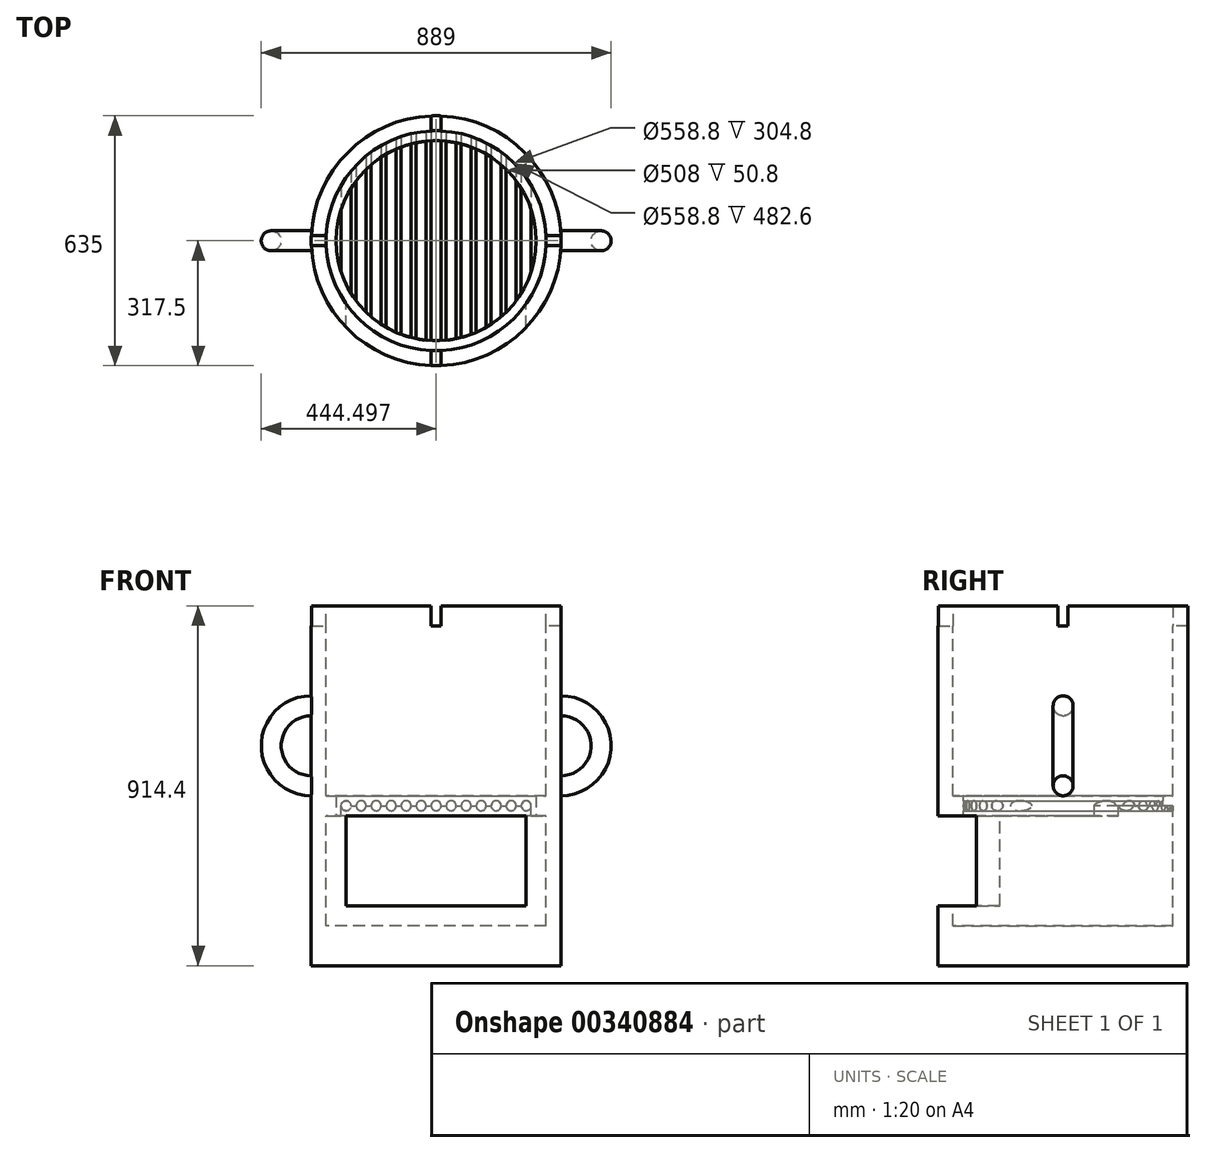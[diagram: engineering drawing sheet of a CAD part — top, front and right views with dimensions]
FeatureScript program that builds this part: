
annotation { "Feature Type Name" : "Feature", "Feature Type Description" : "" }
export const myFeature = defineFeature(function(context is Context, id is Id, definition is map)
    precondition{}
    {
        {
            var Q0;
            Q0=qCreatedBy(makeId("Top.planeOp"),FACE);
            var sketch = newSketch(context, id + "F0", { "sketchPlane" : qUnion([Q0])});
            skCircle(sketch, "E0", {"center": v(0, 0) * mm, "radius": 158.75 * mm});
            skSolve(sketch);
        }
        {
            var Q0;
            Q0=makeQuery(id+"F0.imprint","IMPRINT",FACE,{"disambiguationData":[TD([[makeQuery(id+"F0.imprint","IMPRINT",EDGE,{"derivedFrom":sQuery(id+"F0.wireOp",EDGE,"E0")}),1.0]])]});
            extrude(context, id + "F1", {"entities" : qUnion([Q0]), "depth" : 457.2 * mm});
        }
        {
            var Q0;
            Q0=makeQuery(id+"F1.opExtrude","CAP_FACE",FACE,{"disambiguationData":[OSD([sQuery(id+"F0.wireOp",EDGE,"E0")])],"isStart":false});
            var sketch = newSketch(context, id + "F2", { "sketchPlane" : qUnion([Q0])});
            skPoint(sketch, "E1.0", {"position": v(0, 0) * mm});
            skCircle(sketch, "E2", {"center": v(0, 0) * mm, "radius": 139.7 * mm});
            skSolve(sketch);
        }
        {
            var Q0;
            Q0=makeQuery(id+"F2.imprint","IMPRINT",FACE,{"disambiguationData":[TD([[makeQuery(id+"F2.imprint","IMPRINT",EDGE,{"derivedFrom":sQuery(id+"F2.wireOp",EDGE,"E2")}),1.0]])]});
            extrude(context, id + "F3", {"entities" : qUnion([Q0]), "operationType" : NewBodyOperationType.REMOVE, "oppositeDirection" : true, "depth" : 406.4 * mm});
        }
        {
            var Q0;
            Q0=qCreatedBy(makeId("Front.planeOp"),FACE);
            var sketch = newSketch(context, id + "F4", { "sketchPlane" : qUnion([Q0])});
            skLineSegment(sketch, "E3", {"start": v(-158.75, 0) * mm, "end": v(-158.75, 457.2) * mm});
            skLineSegment(sketch, "E4", {"start": v(158.75, 457.2) * mm, "end": v(158.75, 0) * mm});
            skLineSegment(sketch, "E5", {"start": v(158.75, 457.2) * mm, "end": v(-158.75, 457.2) * mm});
            skLineSegment(sketch, "E6", {"start": v(158.75, 0) * mm, "end": v(-158.75, 0) * mm});
            skPoint(sketch, "E7", {"position": v(0, 0) * mm});
            skLineSegment(sketch, "E8", {"start": v(0, 457.2) * mm, "end": v(0, 0) * mm, "construction": true});
            skLineSegment(sketch, "E9.bottom", {"start": v(114.3, 203.2) * mm, "end": v(-114.3, 203.2) * mm});
            skLineSegment(sketch, "E9.top", {"start": v(114.3, 76.2) * mm, "end": v(-114.3, 76.2) * mm});
            skLineSegment(sketch, "E9.left", {"start": v(114.3, 203.2) * mm, "end": v(114.3, 76.2) * mm});
            skLineSegment(sketch, "E9.right", {"start": v(-114.3, 203.2) * mm, "end": v(-114.3, 76.2) * mm});
            skPoint(sketch, "E10", {"position": v(-514.73, 96.28) * mm});
            skSolve(sketch);
        }
        {
            var Q0;
            Q0=makeQuery(id+"F4.imprint","IMPRINT",FACE,{"disambiguationData":[TD([[makeQuery(id+"F4.imprint","IMPRINT",EDGE,{"derivedFrom":sQuery(id+"F4.wireOp",EDGE,"E9.bottom")}),1.0]])]});
            extrude(context, id + "F5", {"entities" : qUnion([Q0]), "operationType" : NewBodyOperationType.REMOVE, "depth" : 177.8 * mm});
        }
        {
            var Q0;
            Q0=makeQuery(id+"F1.opExtrude","CAP_FACE",FACE,{"disambiguationData":[OSD([sQuery(id+"F0.wireOp",EDGE,"E0")])],"isStart":false});
            var sketch = newSketch(context, id + "F6", { "sketchPlane" : qUnion([Q0])});
            skCircle(sketch, "E11.0.0", {"center": v(0, 0) * mm, "radius": 158.75 * mm, "construction": true});
            skCircle(sketch, "E12.0", {"center": v(0, 0) * mm, "radius": 139.7 * mm, "construction": true});
            skLineSegment(sketch, "E13", {"start": v(-158.75, 0) * mm, "end": v(158.75, 0) * mm, "construction": true});
            skLineSegment(sketch, "E14", {"start": v(0, 158.75) * mm, "end": v(0, -158.75) * mm, "construction": true});
            skLineSegment(sketch, "E15.bottom", {"start": v(-6.35, 158.75) * mm, "end": v(6.35, 158.75) * mm});
            skLineSegment(sketch, "E15.top", {"start": v(-6.35, 139.56) * mm, "end": v(6.35, 139.56) * mm});
            skLineSegment(sketch, "E15.left", {"start": v(-6.35, 158.75) * mm, "end": v(-6.35, 139.56) * mm});
            skLineSegment(sketch, "E15.right", {"start": v(6.35, 158.75) * mm, "end": v(6.35, 139.56) * mm});
            skLineSegment(sketch, "E16.bottom", {"start": v(-158.75, -6.35) * mm, "end": v(-139.56, -6.35) * mm});
            skLineSegment(sketch, "E16.top", {"start": v(-158.75, 6.35) * mm, "end": v(-139.56, 6.35) * mm});
            skLineSegment(sketch, "E16.left", {"start": v(-158.75, -6.35) * mm, "end": v(-158.75, 6.35) * mm});
            skLineSegment(sketch, "E16.right", {"start": v(-139.56, -6.35) * mm, "end": v(-139.56, 6.35) * mm});
            skLineSegment(sketch, "E17.bottom", {"start": v(158.75, 6.35) * mm, "end": v(139.56, 6.35) * mm});
            skLineSegment(sketch, "E17.top", {"start": v(158.75, -6.35) * mm, "end": v(139.56, -6.35) * mm});
            skLineSegment(sketch, "E17.left", {"start": v(158.75, 6.35) * mm, "end": v(158.75, -6.35) * mm});
            skLineSegment(sketch, "E17.right", {"start": v(139.56, 6.35) * mm, "end": v(139.56, -6.35) * mm});
            skLineSegment(sketch, "E18.bottom", {"start": v(6.35, -158.75) * mm, "end": v(-6.35, -158.75) * mm});
            skLineSegment(sketch, "E18.top", {"start": v(6.35, -139.56) * mm, "end": v(-6.35, -139.56) * mm});
            skLineSegment(sketch, "E18.left", {"start": v(6.35, -158.75) * mm, "end": v(6.35, -139.56) * mm});
            skLineSegment(sketch, "E18.right", {"start": v(-6.35, -158.75) * mm, "end": v(-6.35, -139.56) * mm});
            skSolve(sketch);
        }
        {
            var Q0;
            {var subQ0=makeQuery(id+"F1.opExtrude","CAP_EDGE",EDGE,{"disambiguationData":[OSD([sQuery(id+"F0.wireOp",EDGE,"E0")])],"isStart":false});var subQ1=makeQuery(id+"F6.imprint","INTERSECT",VERTEX,{"derivedFrom":[subQ0,sQuery(id+"F6.wireOp",EDGE,"E15.bottom")]});Q0=makeQuery(id+"F6.imprint","IMPRINT",FACE,{"disambiguationData":[TD([[makeQuery(id+"F6.imprint","IMPRINT",EDGE,{"disambiguationData":[TD([[subQ1,-1.0]])],"derivedFrom":subQ0}),1.0]])]});}
            var Q1;
            {var subQ0=sQuery(id+"F6.wireOp",EDGE,"E16.bottom");var subQ1=makeQuery(id+"F1.opExtrude","CAP_EDGE",EDGE,{"disambiguationData":[OSD([sQuery(id+"F0.wireOp",EDGE,"E0")])],"isStart":false});var subQ2=makeQuery(id+"F6.imprint","INTERSECT",VERTEX,{"derivedFrom":[subQ1,subQ0]});Q1=makeQuery(id+"F6.imprint","IMPRINT",FACE,{"disambiguationData":[TD([[makeQuery(id+"F6.imprint","IMPRINT",EDGE,{"disambiguationData":[TD([[subQ2,1.0]])],"derivedFrom":subQ1}),1.0]])]});}
            var Q2;
            {var subQ0=makeQuery(id+"F1.opExtrude","CAP_EDGE",EDGE,{"disambiguationData":[OSD([sQuery(id+"F0.wireOp",EDGE,"E0")])],"isStart":false});var subQ1=makeQuery(id+"F6.imprint","INTERSECT",VERTEX,{"derivedFrom":[subQ0,sQuery(id+"F6.wireOp",EDGE,"E18.bottom")]});Q2=makeQuery(id+"F6.imprint","IMPRINT",FACE,{"disambiguationData":[TD([[makeQuery(id+"F6.imprint","IMPRINT",EDGE,{"disambiguationData":[TD([[subQ1,-1.0]])],"derivedFrom":subQ0}),1.0]])]});}
            var Q3;
            {var subQ0=sQuery(id+"F6.wireOp",EDGE,"E17.bottom");var subQ1=makeQuery(id+"F1.opExtrude","CAP_EDGE",EDGE,{"disambiguationData":[OSD([sQuery(id+"F0.wireOp",EDGE,"E0")])],"isStart":false});var subQ2=makeQuery(id+"F6.imprint","INTERSECT",VERTEX,{"derivedFrom":[subQ1,subQ0]});Q3=makeQuery(id+"F6.imprint","IMPRINT",FACE,{"disambiguationData":[TD([[makeQuery(id+"F6.imprint","IMPRINT",EDGE,{"disambiguationData":[TD([[subQ2,1.0]])],"derivedFrom":subQ1}),1.0]])]});}
            extrude(context, id + "F7", {"entities" : qUnion([Q0, Q1, Q2, Q3]), "operationType" : NewBodyOperationType.REMOVE, "oppositeDirection" : true, "depth" : 25.4 * mm});
        }
        {
            var Q0;
            Q0=makeQuery(id+"F5.boolean.opBoolean","COPY",FACE,{"derivedFrom":makeQuery(id+"F5.opExtrude","SWEPT_FACE",FACE,{"disambiguationData":[OSD([sQuery(id+"F4.wireOp",EDGE,"E9.bottom")])]})});
            var sketch = newSketch(context, id + "F8", { "sketchPlane" : qUnion([Q0])});
            skCircle(sketch, "E19.0.0", {"center": v(0, 0) * mm, "radius": 139.7 * mm});
            skLineSegment(sketch, "E20.0.0", {"start": v(139.56, 6.35) * mm, "end": v(158.62, 6.35) * mm});
            skArc(sketch, "E20.0.1", {"start": v(158.62, 6.35) * mm, "mid": v(158.72, 3.18) * mm, "end": v(158.75, 0) * mm});
            skArc(sketch, "E20.0.2", {"start": v(158.75, 0) * mm, "mid": v(158.72, -3.18) * mm, "end": v(158.62, -6.35) * mm});
            skLineSegment(sketch, "E20.0.3", {"start": v(158.62, -6.35) * mm, "end": v(139.56, -6.35) * mm});
            skArc(sketch, "E20.0.4", {"start": v(139.56, -6.35) * mm, "mid": v(139.7, 0) * mm, "end": v(139.56, 6.35) * mm});
            skLineSegment(sketch, "E21.0.0", {"start": v(6.35, -139.56) * mm, "end": v(6.35, -158.62) * mm});
            skArc(sketch, "E21.0.1", {"start": v(6.35, -158.62) * mm, "mid": v(3.18, -158.72) * mm, "end": v(0, -158.75) * mm});
            skArc(sketch, "E21.0.2", {"start": v(0, -158.75) * mm, "mid": v(-3.18, -158.72) * mm, "end": v(-6.35, -158.62) * mm});
            skLineSegment(sketch, "E21.0.3", {"start": v(-6.35, -158.62) * mm, "end": v(-6.35, -139.56) * mm});
            skArc(sketch, "E21.0.4", {"start": v(-6.35, -139.56) * mm, "mid": v(0, -139.7) * mm, "end": v(6.35, -139.56) * mm});
            skLineSegment(sketch, "E22.0.0", {"start": v(-6.35, 139.56) * mm, "end": v(-6.35, 158.62) * mm});
            skArc(sketch, "E22.0.1", {"start": v(-6.35, 158.62) * mm, "mid": v(-3.18, 158.72) * mm, "end": v(0, 158.75) * mm});
            skArc(sketch, "E22.0.2", {"start": v(0, 158.75) * mm, "mid": v(3.18, 158.72) * mm, "end": v(6.35, 158.62) * mm});
            skLineSegment(sketch, "E22.0.3", {"start": v(6.35, 158.62) * mm, "end": v(6.35, 139.56) * mm});
            skArc(sketch, "E22.0.4", {"start": v(6.35, 139.56) * mm, "mid": v(0, 139.7) * mm, "end": v(-6.35, 139.56) * mm});
            skLineSegment(sketch, "E23.0.0", {"start": v(-139.56, -6.35) * mm, "end": v(-158.62, -6.35) * mm});
            skArc(sketch, "E23.0.1", {"start": v(-158.62, -6.35) * mm, "mid": v(-158.72, -3.18) * mm, "end": v(-158.75, 0) * mm});
            skArc(sketch, "E23.0.2", {"start": v(-158.75, 0) * mm, "mid": v(-158.72, 3.18) * mm, "end": v(-158.62, 6.35) * mm});
            skLineSegment(sketch, "E23.0.3", {"start": v(-158.62, 6.35) * mm, "end": v(-139.56, 6.35) * mm});
            skArc(sketch, "E23.0.4", {"start": v(-139.56, 6.35) * mm, "mid": v(-139.7, 0) * mm, "end": v(-139.56, -6.35) * mm});
            skLineSegment(sketch, "E24", {"start": v(-139.56, 0) * mm, "end": v(139.7, 0) * mm, "construction": true});
            skPoint(sketch, "E24.startSnap0", {"position": v(-139.7, 0) * mm});
            skCircle(sketch, "E25", {"center": v(0, 0) * mm, "radius": 127 * mm});
            skLineSegment(sketch, "E26", {"start": v(0, 127) * mm, "end": v(0, -127) * mm});
            skPoint(sketch, "E27", {"position": v(127, 0) * mm});
            skPoint(sketch, "E28", {"position": v(-127, 0) * mm});
            skPoint(sketch, "E29", {"position": v(-76.2, 0) * mm});
            skPoint(sketch, "E30", {"position": v(-19.05, 0) * mm});
            skPoint(sketch, "E31", {"position": v(-38.1, 0) * mm});
            skPoint(sketch, "E32", {"position": v(-57.15, 0) * mm});
            skPoint(sketch, "E33", {"position": v(-95.25, 0) * mm});
            skPoint(sketch, "E34", {"position": v(-114.3, 0) * mm});
            skLineSegment(sketch, "E35", {"start": v(-114.3, 55.36) * mm, "end": v(-114.3, -55.36) * mm});
            skLineSegment(sketch, "E36", {"start": v(-95.25, 84) * mm, "end": v(-95.25, -84) * mm});
            skLineSegment(sketch, "E37", {"start": v(-76.2, 101.6) * mm, "end": v(-76.2, -101.6) * mm});
            skLineSegment(sketch, "E38", {"start": v(-57.15, -113.41) * mm, "end": v(-57.15, 113.41) * mm});
            skLineSegment(sketch, "E39", {"start": v(-38.1, -121.15) * mm, "end": v(-38.1, 121.15) * mm});
            skLineSegment(sketch, "E40", {"start": v(-19.05, -125.56) * mm, "end": v(-19.05, 125.56) * mm});
            skLineSegment(sketch, "E41.MirrorCS", {"start": v(0, -121.15) * mm, "end": v(0, 121.15) * mm});
            skLineSegment(sketch, "E42.MirrorCS", {"start": v(19.05, -125.56) * mm, "end": v(19.05, 125.56) * mm});
            skLineSegment(sketch, "E43.MirrorCS", {"start": v(38.1, -121.15) * mm, "end": v(38.1, 121.15) * mm});
            skLineSegment(sketch, "E44.MirrorCS", {"start": v(57.15, -113.41) * mm, "end": v(57.15, 113.41) * mm});
            skLineSegment(sketch, "E45.MirrorCS", {"start": v(76.2, 101.6) * mm, "end": v(76.2, -101.6) * mm});
            skLineSegment(sketch, "E46.MirrorCS", {"start": v(95.25, 84) * mm, "end": v(95.25, -84) * mm});
            skLineSegment(sketch, "E47.MirrorCS", {"start": v(114.3, 55.36) * mm, "end": v(114.3, -55.36) * mm});
            skSolve(sketch);
        }
        {
            var Q0;
            {var subQ17=sQuery(id+"F8.wireOp",EDGE,"E19.0.0");var subQ19=makeQuery(id+"F8.imprint","INTERSECT",VERTEX,{"derivedFrom":[subQ17,sQuery(id+"F8.wireOp",EDGE,"E23.0.0")]});Q0=makeQuery(id+"F8.imprint","IMPRINT",FACE,{"disambiguationData":[TD([[makeQuery(id+"F8.imprint","IMPRINT",EDGE,{"disambiguationData":[TD([[subQ19,1.0]])],"derivedFrom":subQ17}),1.0]])]});}
            extrude(context, id + "F9", {"entities" : qUnion([Q0]), "operationType" : NewBodyOperationType.ADD, "oppositeDirection" : true, "depth" : 12.7 * mm});
        }
        {
            var Q0;
            Q0=qCreatedBy(makeId("Front.planeOp"),FACE);
            var sketch = newSketch(context, id + "F10", { "sketchPlane" : qUnion([Q0])});
            skPoint(sketch, "E48.0", {"position": v(-114.3, 203.2) * mm});
            skPoint(sketch, "E49.0", {"position": v(-95.25, 203.2) * mm});
            skPoint(sketch, "E50.0", {"position": v(-76.2, 203.2) * mm});
            skPoint(sketch, "E51.0", {"position": v(-57.15, 203.2) * mm});
            skPoint(sketch, "E52.0", {"position": v(-38.1, 203.2) * mm});
            skPoint(sketch, "E53.0", {"position": v(-19.05, 203.2) * mm});
            skPoint(sketch, "E54.0", {"position": v(0, 203.2) * mm});
            skPoint(sketch, "E55.0", {"position": v(19.05, 203.2) * mm});
            skPoint(sketch, "E56.0", {"position": v(38.1, 203.2) * mm});
            skPoint(sketch, "E57.0", {"position": v(57.15, 203.2) * mm});
            skPoint(sketch, "E58.0", {"position": v(76.2, 203.2) * mm});
            skPoint(sketch, "E59.0", {"position": v(95.25, 203.2) * mm});
            skPoint(sketch, "E60.0", {"position": v(114.3, 203.2) * mm});
            skCircle(sketch, "E61", {"center": v(-114.3, 203.2) * mm, "radius": 6.35 * mm});
            skCircle(sketch, "E62", {"center": v(-95.25, 203.2) * mm, "radius": 6.35 * mm});
            skCircle(sketch, "E63", {"center": v(-76.2, 203.2) * mm, "radius": 6.35 * mm});
            skCircle(sketch, "E64", {"center": v(-57.15, 203.2) * mm, "radius": 6.35 * mm});
            skCircle(sketch, "E65", {"center": v(-38.1, 203.2) * mm, "radius": 6.35 * mm});
            skCircle(sketch, "E66", {"center": v(-19.05, 203.2) * mm, "radius": 6.35 * mm});
            skCircle(sketch, "E67", {"center": v(0, 203.2) * mm, "radius": 6.35 * mm});
            skCircle(sketch, "E68", {"center": v(19.05, 203.2) * mm, "radius": 6.35 * mm});
            skCircle(sketch, "E69", {"center": v(38.1, 203.2) * mm, "radius": 6.35 * mm});
            skCircle(sketch, "E70", {"center": v(57.15, 203.2) * mm, "radius": 6.35 * mm});
            skCircle(sketch, "E71", {"center": v(76.2, 203.2) * mm, "radius": 6.35 * mm});
            skCircle(sketch, "E72", {"center": v(95.25, 203.2) * mm, "radius": 6.35 * mm});
            skCircle(sketch, "E73", {"center": v(114.3, 203.2) * mm, "radius": 6.35 * mm});
            skSolve(sketch);
        }
        {
            var Q0;
            Q0=makeQuery(id+"F10.imprint","IMPRINT",FACE,{"disambiguationData":[TD([[makeQuery(id+"F10.imprint","IMPRINT",EDGE,{"derivedFrom":sQuery(id+"F10.wireOp",EDGE,"E61")}),1.0]])]});
            var Q1;
            Q1=makeQuery(id+"F10.imprint","IMPRINT",FACE,{"disambiguationData":[TD([[makeQuery(id+"F10.imprint","IMPRINT",EDGE,{"derivedFrom":sQuery(id+"F10.wireOp",EDGE,"E66")}),1.0]])]});
            var Q2;
            Q2=makeQuery(id+"F10.imprint","IMPRINT",FACE,{"disambiguationData":[TD([[makeQuery(id+"F10.imprint","IMPRINT",EDGE,{"derivedFrom":sQuery(id+"F10.wireOp",EDGE,"E62")}),1.0]])]});
            var Q3;
            Q3=makeQuery(id+"F10.imprint","IMPRINT",FACE,{"disambiguationData":[TD([[makeQuery(id+"F10.imprint","IMPRINT",EDGE,{"derivedFrom":sQuery(id+"F10.wireOp",EDGE,"E63")}),1.0]])]});
            var Q4;
            Q4=makeQuery(id+"F10.imprint","IMPRINT",FACE,{"disambiguationData":[TD([[makeQuery(id+"F10.imprint","IMPRINT",EDGE,{"derivedFrom":sQuery(id+"F10.wireOp",EDGE,"E65")}),1.0]])]});
            var Q5;
            Q5=makeQuery(id+"F10.imprint","IMPRINT",FACE,{"disambiguationData":[TD([[makeQuery(id+"F10.imprint","IMPRINT",EDGE,{"derivedFrom":sQuery(id+"F10.wireOp",EDGE,"E64")}),1.0]])]});
            var Q6;
            Q6=makeQuery(id+"F10.imprint","IMPRINT",FACE,{"disambiguationData":[TD([[makeQuery(id+"F10.imprint","IMPRINT",EDGE,{"derivedFrom":sQuery(id+"F10.wireOp",EDGE,"E72")}),1.0]])]});
            var Q7;
            Q7=makeQuery(id+"F10.imprint","IMPRINT",FACE,{"disambiguationData":[TD([[makeQuery(id+"F10.imprint","IMPRINT",EDGE,{"derivedFrom":sQuery(id+"F10.wireOp",EDGE,"E71")}),1.0]])]});
            var Q8;
            Q8=makeQuery(id+"F10.imprint","IMPRINT",FACE,{"disambiguationData":[TD([[makeQuery(id+"F10.imprint","IMPRINT",EDGE,{"derivedFrom":sQuery(id+"F10.wireOp",EDGE,"E70")}),1.0]])]});
            var Q9;
            Q9=makeQuery(id+"F10.imprint","IMPRINT",FACE,{"disambiguationData":[TD([[makeQuery(id+"F10.imprint","IMPRINT",EDGE,{"derivedFrom":sQuery(id+"F10.wireOp",EDGE,"E69")}),1.0]])]});
            var Q10;
            Q10=makeQuery(id+"F10.imprint","IMPRINT",FACE,{"disambiguationData":[TD([[makeQuery(id+"F10.imprint","IMPRINT",EDGE,{"derivedFrom":sQuery(id+"F10.wireOp",EDGE,"E68")}),1.0]])]});
            var Q11;
            Q11=makeQuery(id+"F10.imprint","IMPRINT",FACE,{"disambiguationData":[TD([[makeQuery(id+"F10.imprint","IMPRINT",EDGE,{"derivedFrom":sQuery(id+"F10.wireOp",EDGE,"E67")}),1.0]])]});
            var Q12;
            Q12=makeQuery(id+"F10.imprint","IMPRINT",FACE,{"disambiguationData":[TD([[makeQuery(id+"F10.imprint","IMPRINT",EDGE,{"derivedFrom":sQuery(id+"F10.wireOp",EDGE,"E73")}),1.0]])]});
            var Q13;
            Q13=makeQuery(id+"F9.opExtrude","SWEPT_FACE",FACE,{"disambiguationData":[OSD([sQuery(id+"F8.wireOp",EDGE,"E25")])]});
            extrude(context, id + "F11", {"entities" : qUnion([Q0, Q1, Q2, Q3, Q4, Q5, Q6, Q7, Q8, Q9, Q10, Q11, Q12]), "operationType" : NewBodyOperationType.ADD, "endBound" : BoundingType.UP_TO_SURFACE, "endBoundEntityFace" : qUnion([Q13]), "depth" : 228.6 * mm});
        }
        {
            var Q0;
            Q0=makeQuery(id+"F10.imprint","IMPRINT",FACE,{"disambiguationData":[TD([[makeQuery(id+"F10.imprint","IMPRINT",EDGE,{"derivedFrom":sQuery(id+"F10.wireOp",EDGE,"E73")}),1.0]])]});
            var Q1;
            Q1=makeQuery(id+"F10.imprint","IMPRINT",FACE,{"disambiguationData":[TD([[makeQuery(id+"F10.imprint","IMPRINT",EDGE,{"derivedFrom":sQuery(id+"F10.wireOp",EDGE,"E72")}),1.0]])]});
            var Q2;
            Q2=makeQuery(id+"F10.imprint","IMPRINT",FACE,{"disambiguationData":[TD([[makeQuery(id+"F10.imprint","IMPRINT",EDGE,{"derivedFrom":sQuery(id+"F10.wireOp",EDGE,"E71")}),1.0]])]});
            var Q3;
            Q3=makeQuery(id+"F10.imprint","IMPRINT",FACE,{"disambiguationData":[TD([[makeQuery(id+"F10.imprint","IMPRINT",EDGE,{"derivedFrom":sQuery(id+"F10.wireOp",EDGE,"E70")}),1.0]])]});
            var Q4;
            Q4=makeQuery(id+"F10.imprint","IMPRINT",FACE,{"disambiguationData":[TD([[makeQuery(id+"F10.imprint","IMPRINT",EDGE,{"derivedFrom":sQuery(id+"F10.wireOp",EDGE,"E69")}),1.0]])]});
            var Q5;
            Q5=makeQuery(id+"F10.imprint","IMPRINT",FACE,{"disambiguationData":[TD([[makeQuery(id+"F10.imprint","IMPRINT",EDGE,{"derivedFrom":sQuery(id+"F10.wireOp",EDGE,"E68")}),1.0]])]});
            var Q6;
            Q6=makeQuery(id+"F10.imprint","IMPRINT",FACE,{"disambiguationData":[TD([[makeQuery(id+"F10.imprint","IMPRINT",EDGE,{"derivedFrom":sQuery(id+"F10.wireOp",EDGE,"E67")}),1.0]])]});
            var Q7;
            Q7=makeQuery(id+"F10.imprint","IMPRINT",FACE,{"disambiguationData":[TD([[makeQuery(id+"F10.imprint","IMPRINT",EDGE,{"derivedFrom":sQuery(id+"F10.wireOp",EDGE,"E61")}),1.0]])]});
            var Q8;
            Q8=makeQuery(id+"F10.imprint","IMPRINT",FACE,{"disambiguationData":[TD([[makeQuery(id+"F10.imprint","IMPRINT",EDGE,{"derivedFrom":sQuery(id+"F10.wireOp",EDGE,"E66")}),1.0]])]});
            var Q9;
            Q9=makeQuery(id+"F10.imprint","IMPRINT",FACE,{"disambiguationData":[TD([[makeQuery(id+"F10.imprint","IMPRINT",EDGE,{"derivedFrom":sQuery(id+"F10.wireOp",EDGE,"E62")}),1.0]])]});
            var Q10;
            Q10=makeQuery(id+"F10.imprint","IMPRINT",FACE,{"disambiguationData":[TD([[makeQuery(id+"F10.imprint","IMPRINT",EDGE,{"derivedFrom":sQuery(id+"F10.wireOp",EDGE,"E63")}),1.0]])]});
            var Q11;
            Q11=makeQuery(id+"F10.imprint","IMPRINT",FACE,{"disambiguationData":[TD([[makeQuery(id+"F10.imprint","IMPRINT",EDGE,{"derivedFrom":sQuery(id+"F10.wireOp",EDGE,"E65")}),1.0]])]});
            var Q12;
            Q12=makeQuery(id+"F10.imprint","IMPRINT",FACE,{"disambiguationData":[TD([[makeQuery(id+"F10.imprint","IMPRINT",EDGE,{"derivedFrom":sQuery(id+"F10.wireOp",EDGE,"E64")}),1.0]])]});
            extrude(context, id + "F12", {"entities" : qUnion([Q0, Q1, Q2, Q3, Q4, Q5, Q6, Q7, Q8, Q9, Q10, Q11, Q12]), "operationType" : NewBodyOperationType.ADD, "endBound" : BoundingType.UP_TO_NEXT, "oppositeDirection" : true, "depth" : 25.4 * mm});
        }
        {
            var Q0;
            {var subQ0=sQuery(id+"F10.wireOp",EDGE,"E63");var subQ1=sQuery(id+"F8.wireOp",EDGE,"E25");var subQ2=sQuery(id+"F10.wireOp",EDGE,"E73");var subQ3=sQuery(id+"F10.wireOp",EDGE,"E72");var subQ4=sQuery(id+"F10.wireOp",EDGE,"E71");var subQ5=sQuery(id+"F10.wireOp",EDGE,"E69");var subQ6=sQuery(id+"F10.wireOp",EDGE,"E68");var subQ7=sQuery(id+"F10.wireOp",EDGE,"E67");var subQ8=sQuery(id+"F10.wireOp",EDGE,"E66");var subQ9=sQuery(id+"F10.wireOp",EDGE,"E61");var subQ10=sQuery(id+"F10.wireOp",EDGE,"E64");var subQ11=sQuery(id+"F10.wireOp",EDGE,"E70");var subQ12=sQuery(id+"F10.wireOp",EDGE,"E62");var subQ13=sQuery(id+"F10.wireOp",EDGE,"E65");Q0=makeQuery(id+"F12.boolean.opBoolean","SPLIT",FACE,{"disambiguationData":[TD([makeQuery(id+"F1.opExtrude","SWEPT_FACE",FACE,{"disambiguationData":[OSD([sQuery(id+"F0.wireOp",EDGE,"E0")])]}),makeQuery(id+"F3.boolean.opBoolean","COPY",FACE,{"derivedFrom":makeQuery(id+"F3.opExtrude","SWEPT_FACE",FACE,{"disambiguationData":[OSD([sQuery(id+"F2.wireOp",EDGE,"E2")])]})}),makeQuery(id+"F5.boolean.opBoolean","COPY",FACE,{"derivedFrom":makeQuery(id+"F5.opExtrude","SWEPT_FACE",FACE,{"disambiguationData":[OSD([sQuery(id+"F4.wireOp",EDGE,"E9.left")])]})}),makeQuery(id+"F5.boolean.opBoolean","COPY",FACE,{"derivedFrom":makeQuery(id+"F5.opExtrude","SWEPT_FACE",FACE,{"disambiguationData":[OSD([sQuery(id+"F4.wireOp",EDGE,"E9.right")])]})}),makeQuery(id+"F9.opExtrude","SWEPT_FACE",FACE,{"disambiguationData":[OSD([subQ1])]}),makeQuery(id+"F11.opExtrude","SWEPT_FACE",FACE,{"disambiguationData":[OSD([subQ9])]}),makeQuery(id+"F11.opExtrude","SWEPT_FACE",FACE,{"disambiguationData":[OSD([subQ12])]}),makeQuery(id+"F11.opExtrude","SWEPT_FACE",FACE,{"disambiguationData":[OSD([subQ0])]}),makeQuery(id+"F11.opExtrude","SWEPT_FACE",FACE,{"disambiguationData":[OSD([subQ10])]}),makeQuery(id+"F11.opExtrude","SWEPT_FACE",FACE,{"disambiguationData":[OSD([subQ13])]}),makeQuery(id+"F11.opExtrude","SWEPT_FACE",FACE,{"disambiguationData":[OSD([subQ8])]}),makeQuery(id+"F11.opExtrude","SWEPT_FACE",FACE,{"disambiguationData":[OSD([subQ7])]}),makeQuery(id+"F11.opExtrude","SWEPT_FACE",FACE,{"disambiguationData":[OSD([subQ6])]}),makeQuery(id+"F11.opExtrude","SWEPT_FACE",FACE,{"disambiguationData":[OSD([subQ5])]}),makeQuery(id+"F11.opExtrude","SWEPT_FACE",FACE,{"disambiguationData":[OSD([subQ11])]}),makeQuery(id+"F11.opExtrude","SWEPT_FACE",FACE,{"disambiguationData":[OSD([subQ4])]}),makeQuery(id+"F11.opExtrude","SWEPT_FACE",FACE,{"disambiguationData":[OSD([subQ3])]}),makeQuery(id+"F11.opExtrude","SWEPT_FACE",FACE,{"disambiguationData":[OSD([subQ2])]}),makeQuery(id+"F11.opExtrude","CAP_FACE",FACE,{"disambiguationData":[OSD([subQ1]),ownerDisambiguation([makeQuery(id+"F11.opExtrude","SWEPT_BODY",BODY,{"disambiguationData":[OSD([subQ9])]})])],"isStart":false}),makeQuery(id+"F11.opExtrude","CAP_FACE",FACE,{"disambiguationData":[OSD([subQ1]),ownerDisambiguation([makeQuery(id+"F11.opExtrude","SWEPT_BODY",BODY,{"disambiguationData":[OSD([subQ12])]})])],"isStart":false}),makeQuery(id+"F11.opExtrude","CAP_FACE",FACE,{"disambiguationData":[OSD([subQ1]),ownerDisambiguation([makeQuery(id+"F11.opExtrude","SWEPT_BODY",BODY,{"disambiguationData":[OSD([subQ0])]})])],"isStart":false}),makeQuery(id+"F11.opExtrude","CAP_FACE",FACE,{"disambiguationData":[OSD([subQ1]),ownerDisambiguation([makeQuery(id+"F11.opExtrude","SWEPT_BODY",BODY,{"disambiguationData":[OSD([subQ10])]})])],"isStart":false}),makeQuery(id+"F11.opExtrude","CAP_FACE",FACE,{"disambiguationData":[OSD([subQ1]),ownerDisambiguation([makeQuery(id+"F11.opExtrude","SWEPT_BODY",BODY,{"disambiguationData":[OSD([subQ13])]})])],"isStart":false}),makeQuery(id+"F11.opExtrude","CAP_FACE",FACE,{"disambiguationData":[OSD([subQ1]),ownerDisambiguation([makeQuery(id+"F11.opExtrude","SWEPT_BODY",BODY,{"disambiguationData":[OSD([subQ8])]})])],"isStart":false}),makeQuery(id+"F11.opExtrude","CAP_FACE",FACE,{"disambiguationData":[OSD([subQ1]),ownerDisambiguation([makeQuery(id+"F11.opExtrude","SWEPT_BODY",BODY,{"disambiguationData":[OSD([subQ7])]})])],"isStart":false}),makeQuery(id+"F11.opExtrude","CAP_FACE",FACE,{"disambiguationData":[OSD([subQ1]),ownerDisambiguation([makeQuery(id+"F11.opExtrude","SWEPT_BODY",BODY,{"disambiguationData":[OSD([subQ6])]})])],"isStart":false}),makeQuery(id+"F11.opExtrude","CAP_FACE",FACE,{"disambiguationData":[OSD([subQ1]),ownerDisambiguation([makeQuery(id+"F11.opExtrude","SWEPT_BODY",BODY,{"disambiguationData":[OSD([subQ5])]})])],"isStart":false}),makeQuery(id+"F11.opExtrude","CAP_FACE",FACE,{"disambiguationData":[OSD([subQ1]),ownerDisambiguation([makeQuery(id+"F11.opExtrude","SWEPT_BODY",BODY,{"disambiguationData":[OSD([subQ11])]})])],"isStart":false}),makeQuery(id+"F11.opExtrude","CAP_FACE",FACE,{"disambiguationData":[OSD([subQ1]),ownerDisambiguation([makeQuery(id+"F11.opExtrude","SWEPT_BODY",BODY,{"disambiguationData":[OSD([subQ4])]})])],"isStart":false}),makeQuery(id+"F11.opExtrude","CAP_FACE",FACE,{"disambiguationData":[OSD([subQ1]),ownerDisambiguation([makeQuery(id+"F11.opExtrude","SWEPT_BODY",BODY,{"disambiguationData":[OSD([subQ3])]})])],"isStart":false}),makeQuery(id+"F11.opExtrude","CAP_FACE",FACE,{"disambiguationData":[OSD([subQ1]),ownerDisambiguation([makeQuery(id+"F11.opExtrude","SWEPT_BODY",BODY,{"disambiguationData":[OSD([subQ2])]})])],"isStart":false}),makeQuery(id+"F12.opExtrude","SWEPT_FACE",FACE,{"disambiguationData":[OSD([subQ9])]}),makeQuery(id+"F12.opExtrude","SWEPT_FACE",FACE,{"disambiguationData":[OSD([subQ12])]}),makeQuery(id+"F12.opExtrude","SWEPT_FACE",FACE,{"disambiguationData":[OSD([subQ0])]}),makeQuery(id+"F12.opExtrude","SWEPT_FACE",FACE,{"disambiguationData":[OSD([subQ10])]}),makeQuery(id+"F12.opExtrude","SWEPT_FACE",FACE,{"disambiguationData":[OSD([subQ13])]}),makeQuery(id+"F12.opExtrude","SWEPT_FACE",FACE,{"disambiguationData":[OSD([subQ8])]}),makeQuery(id+"F12.opExtrude","SWEPT_FACE",FACE,{"disambiguationData":[OSD([subQ7])]}),makeQuery(id+"F12.opExtrude","SWEPT_FACE",FACE,{"disambiguationData":[OSD([subQ6])]}),makeQuery(id+"F12.opExtrude","SWEPT_FACE",FACE,{"disambiguationData":[OSD([subQ5])]}),makeQuery(id+"F12.opExtrude","SWEPT_FACE",FACE,{"disambiguationData":[OSD([subQ11])]}),makeQuery(id+"F12.opExtrude","SWEPT_FACE",FACE,{"disambiguationData":[OSD([subQ4])]}),makeQuery(id+"F12.opExtrude","SWEPT_FACE",FACE,{"disambiguationData":[OSD([subQ3])]}),makeQuery(id+"F12.opExtrude","SWEPT_FACE",FACE,{"disambiguationData":[OSD([subQ2])]})])],"derivedFrom":makeQuery(id+"F9.boolean.opBoolean","MERGE",FACE,{"derivedFrom":[makeQuery(id+"F5.boolean.opBoolean","COPY",FACE,{"derivedFrom":makeQuery(id+"F5.opExtrude","SWEPT_FACE",FACE,{"disambiguationData":[OSD([sQuery(id+"F4.wireOp",EDGE,"E9.bottom")])]})}),makeQuery(id+"F9.opExtrude","CAP_FACE",FACE,{"disambiguationData":[OSD([sQuery(id+"F8.wireOp",EDGE,"E19.0.0"),subQ1])],"isStart":true})]})});}
            extrude(context, id + "F13", {"entities" : qUnion([Q0]), "operationType" : NewBodyOperationType.ADD, "depth" : 12.7 * mm});
        }
        {
            var Q0;
            Q0=sQuery(id+"F6.wireOp",VERTEX,"E13.start");
            var Q1;
            Q1=qCreatedBy(makeId("Right.planeOp"),FACE);
            cPlane(context, id + "F14", {"entities" : qUnion([Q0, Q1]), "cplaneType" : CPlaneType.PLANE_POINT, "offset" : 25.4 * mm, "width" : 152.4 * mm, "height" : 152.4 * mm});
        }
        {
            var Q0;
            Q0=qCreatedBy(id+"F14.planeOp",FACE);
            var sketch = newSketch(context, id + "F15", { "sketchPlane" : qUnion([Q0])});
            skLineSegment(sketch, "E74", {"start": v(-158.75, 0) * mm, "end": v(-158.75, 431.8) * mm, "construction": true});
            skLineSegment(sketch, "E75", {"start": v(158.75, 431.8) * mm, "end": v(158.75, 0) * mm, "construction": true});
            skLineSegment(sketch, "E76.0", {"start": v(-158.75, 457.2) * mm, "end": v(158.75, 457.2) * mm, "construction": true});
            skLineSegment(sketch, "E77.0", {"start": v(-158.75, 0) * mm, "end": v(158.75, 0) * mm, "construction": true});
            skLineSegment(sketch, "E78.0", {"start": v(158.62, 431.8) * mm, "end": v(158.62, 457.2) * mm, "construction": true});
            skLineSegment(sketch, "E79.0", {"start": v(-158.62, 431.8) * mm, "end": v(-158.62, 457.2) * mm, "construction": true});
            skLineSegment(sketch, "E80", {"start": v(0, 457.2) * mm, "end": v(0, 0) * mm, "construction": true});
            skPoint(sketch, "E81", {"position": v(0, 228.6) * mm});
            skSolve(sketch);
        }
        {
            var Q0;
            Q0=sQuery(id+"F15.wireOp",VERTEX,"E81");
            var Q1;
            Q1=qCreatedBy(id+"F14.planeOp",FACE);
            cPlane(context, id + "F16", {"entities" : qUnion([Q0, Q1]), "cplaneType" : CPlaneType.PLANE_POINT, "offset" : 25.4 * mm, "width" : 152.4 * mm, "height" : 152.4 * mm});
        }
        {
            var Q0;
            Q0=sQuery(id+"F15.wireOp",VERTEX,"E81");
            var Q1;
            Q1=qCreatedBy(makeId("Front.planeOp"),FACE);
            cPlane(context, id + "F17", {"entities" : qUnion([Q0, Q1]), "cplaneType" : CPlaneType.PLANE_POINT, "offset" : 25.4 * mm, "width" : 152.4 * mm, "height" : 152.4 * mm});
        }
        {
            var Q0;
            Q0=qCreatedBy(id+"F17.planeOp",FACE);
            var sketch = newSketch(context, id + "F18", { "sketchPlane" : qUnion([Q0])});
            skPoint(sketch, "E82.0", {"position": v(-158.75, 228.6) * mm});
            skLineSegment(sketch, "E83.0", {"start": v(-158.75, 457.2) * mm, "end": v(-158.75, 0) * mm});
            skArc(sketch, "E84", {"start": v(-158.75, 228.6) * mm, "mid": v(-209.55, 279.4) * mm, "end": v(-158.75, 330.2) * mm});
            skSolve(sketch);
        }
        {
            var Q0;
            Q0=qCreatedBy(id+"F16.planeOp",FACE);
            var sketch = newSketch(context, id + "F19", { "sketchPlane" : qUnion([Q0])});
            skPoint(sketch, "E85.0", {"position": v(0, 228.6) * mm});
            skCircle(sketch, "E86", {"center": v(0, 228.6) * mm, "radius": 12.7 * mm});
            skSolve(sketch);
        }
        {
            var Q0;
            Q0=makeQuery(id+"F19.imprint","IMPRINT",FACE,{"disambiguationData":[TD([[makeQuery(id+"F19.imprint","IMPRINT",EDGE,{"derivedFrom":sQuery(id+"F19.wireOp",EDGE,"E86")}),1.0]])]});
            var Q1;
            Q1=sQuery(id+"F18.wireOp",EDGE,"E84");
            sweep(context, id + "F20", {"profiles" : qUnion([Q0]), "path" : qUnion([Q1])});
        }
        {
            var Q0;
            Q0=makeQuery(id+"F20.opSweep","CAP_FACE",FACE,{"disambiguationData":[OSD([sQuery(id+"F18.wireOp",VERTEX,"E84.end"),sQuery(id+"F19.wireOp",EDGE,"E86")])],"isStart":false});
            var Q1;
            Q1=makeQuery(id+"F20.opSweep","CAP_FACE",FACE,{"disambiguationData":[OSD([sQuery(id+"F18.wireOp",VERTEX,"E84.start"),sQuery(id+"F19.wireOp",EDGE,"E86")])],"isStart":true});
            extrude(context, id + "F21", {"entities" : qUnion([Q0, Q1]), "operationType" : NewBodyOperationType.ADD, "depth" : 12.7 * mm});
        }
        {
            var Q0;
            Q0=makeQuery(id+"F1.opExtrude","SWEPT_BODY",BODY,{"disambiguationData":[OSD([sQuery(id+"F0.wireOp",EDGE,"E0")])]});
            var Q1;
            Q1=qCreatedBy(makeId("Right.planeOp"),FACE);
            mirror(context, id + "F22", {"operationType" : NewBodyOperationType.ADD, "entities" : qUnion([Q0]), "mirrorPlane" : qUnion([Q1])});
        }
        {
            var Q0;
            Q0=sQuery(id+"F18.wireOp",VERTEX,"E82.0");
            var Q1;
            Q1=qCreatedBy(makeId("Top.planeOp"),FACE);
            cPlane(context, id + "F23", {"entities" : qUnion([Q0, Q1]), "cplaneType" : CPlaneType.PLANE_POINT, "offset" : 25.4 * mm, "width" : 152.4 * mm, "height" : 152.4 * mm});
        }
        {
            var Q0;
            Q0=qCreatedBy(id+"F23.planeOp",FACE);
            var sketch = newSketch(context, id + "F24", { "sketchPlane" : qUnion([Q0])});
            skPoint(sketch, "E87.0", {"position": v(-158.75, 0) * mm});
            skCircle(sketch, "E88.0", {"center": v(0, 0) * mm, "radius": 158.75 * mm, "construction": true});
            skArc(sketch, "E89", {"start": v(-126.24, -96.26) * mm, "mid": v(-260.35, 0) * mm, "end": v(-126.24, 96.26) * mm});
            skSolve(sketch);
        }
        {
            var Q0;
            Q0=sQuery(id+"F24.wireOp",VERTEX,"E89.end");
            var Q1;
            Q1=qCreatedBy(makeId("Right.planeOp"),FACE);
            cPlane(context, id + "F25", {"entities" : qUnion([Q0, Q1]), "cplaneType" : CPlaneType.PLANE_POINT, "offset" : 25.4 * mm, "width" : 152.4 * mm, "height" : 152.4 * mm});
        }
        {
            var Q0;
            Q0=makeQuery(id+"F1.opExtrude","SWEPT_BODY",BODY,{"disambiguationData":[OSD([sQuery(id+"F0.wireOp",EDGE,"E0")])]});
            var Q1;
            Q1=makeQuery(id+"F7.boolean.opBoolean","COPY",VERTEX,{"derivedFrom":makeQuery(id+"F7.opExtrude","CAP_VERTEX",VERTEX,{"disambiguationData":[OSD([sQuery(id+"F0.wireOp",EDGE,"E0"),sQuery(id+"F6.wireOp",EDGE,"E17.top")])],"isStart":true})});
            transform(context, id + "F26", {"entities" : qUnion([Q0]), "transformType" : TransformType.SCALE_UNIFORMLY, "scale" : 2, "scalePoint" : qUnion([Q1]), "makeCopy" : false});
        }
        {
            var Q0;
            Q0=makeQuery(id+"F1.opExtrude","SWEPT_BODY",BODY,{"disambiguationData":[OSD([sQuery(id+"F0.wireOp",EDGE,"E0")])]});
            transform(context, id + "F27", {"entities" : qUnion([Q0]), "transformType" : TransformType.TRANSLATION_3D, "dx" : 1270 * mm, "dy" : 0 * mm, "dz" : 0 * mm, "makeCopy" : false});
        }
    });
